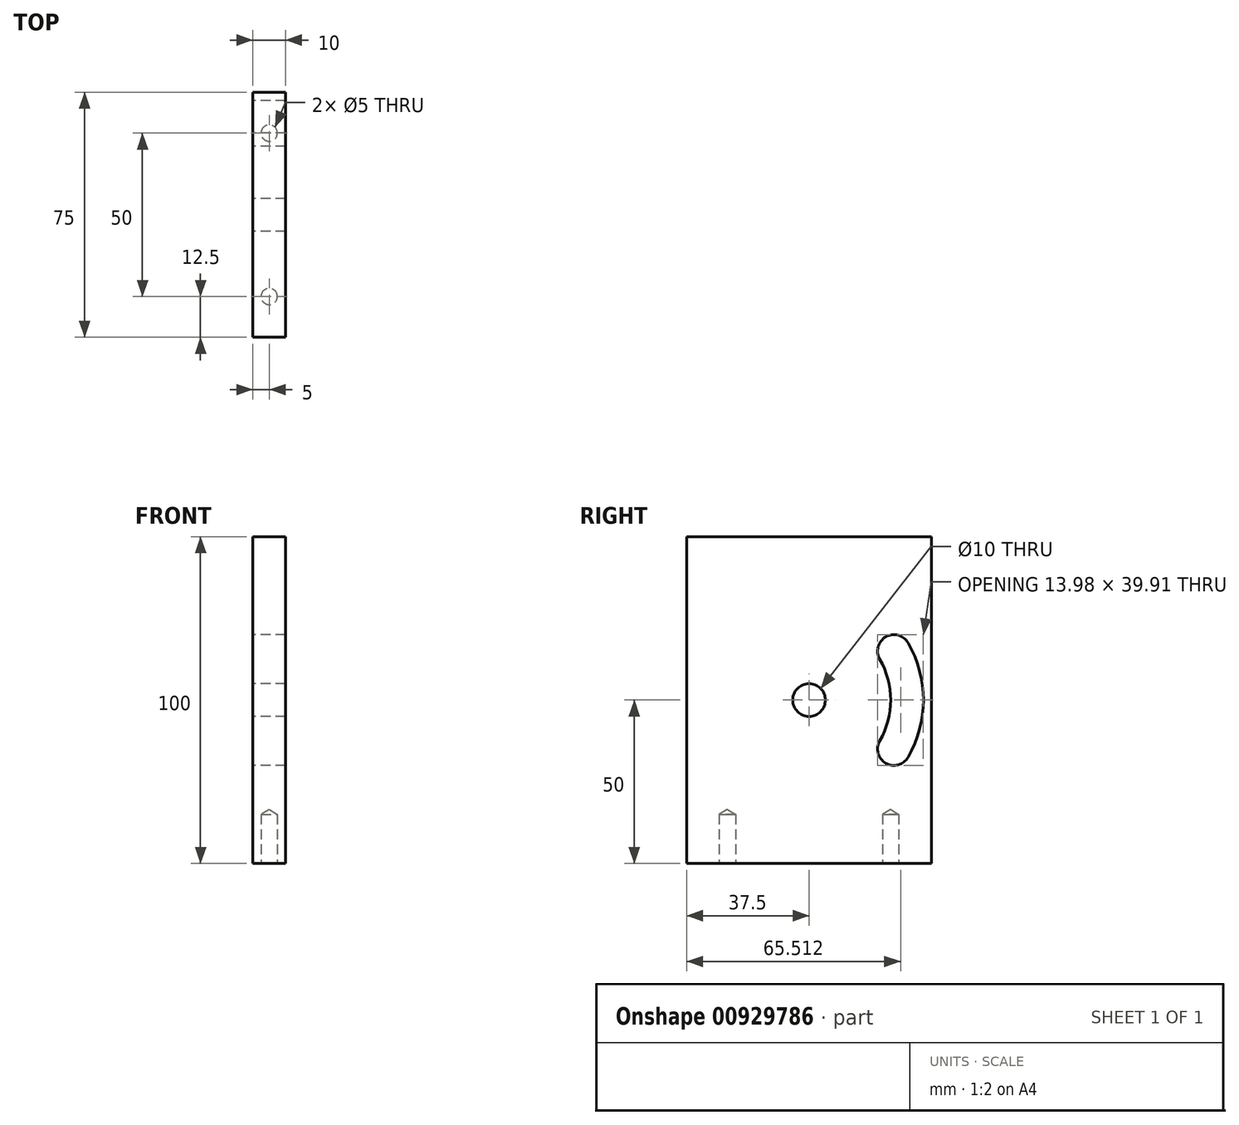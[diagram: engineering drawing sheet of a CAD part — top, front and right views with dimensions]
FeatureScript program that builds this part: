
annotation { "Feature Type Name" : "Feature", "Feature Type Description" : "" }
export const myFeature = defineFeature(function(context is Context, id is Id, definition is map)
    precondition{}
    {
        {
            var Q0;
            Q0=qCreatedBy(makeId("Top.planeOp"),FACE);
            var sketch = newSketch(context, id + "F0", { "sketchPlane" : qUnion([Q0])});
            skLineSegment(sketch, "E0.bottom", {"start": v(5, 37.5) * mm, "end": v(-5, 37.5) * mm});
            skLineSegment(sketch, "E0.top", {"start": v(5, -37.5) * mm, "end": v(-5, -37.5) * mm});
            skLineSegment(sketch, "E0.left", {"start": v(5, 37.5) * mm, "end": v(5, -37.5) * mm});
            skLineSegment(sketch, "E0.right", {"start": v(-5, 37.5) * mm, "end": v(-5, -37.5) * mm});
            skPoint(sketch, "E0.middle", {"position": v(0, 0) * mm});
            skSolve(sketch);
        }
        {
            var Q0;
            Q0 = qSketchRegion(id + "F0", true);
            extrude(context, id + "F1", {"entities" : qUnion([Q0]), "depth" : 100 * mm, "offsetDistance" : 25 * mm});
        }
        {
            var Q0;
            Q0=makeQuery(id+"F1.opExtrude","CAP_FACE",FACE,{"disambiguationData":[OSD([sQuery(id+"F0.wireOp",EDGE,"E0.bottom"),sQuery(id+"F0.wireOp",EDGE,"E0.top"),sQuery(id+"F0.wireOp",EDGE,"E0.left"),sQuery(id+"F0.wireOp",EDGE,"E0.right")])],"isStart":true});
            var sketch = newSketch(context, id + "F2", { "sketchPlane" : qUnion([Q0])});
            skLineSegment(sketch, "E1", {"start": v(0, 37.5) * mm, "end": v(0, -37.5) * mm, "construction": true});
            skLineSegment(sketch, "E2", {"start": v(-5, 0) * mm, "end": v(5, 0) * mm, "construction": true});
            skLineSegment(sketch, "E3.0", {"start": v(-7.5, -25) * mm, "end": v(7.5, -25) * mm, "construction": true});
            skLineSegment(sketch, "E4.0", {"start": v(-7.5, 25) * mm, "end": v(7.5, 25) * mm, "construction": true});
            skCircle(sketch, "E5", {"center": v(0, 25) * mm, "radius": 2.5 * mm});
            skCircle(sketch, "E6", {"center": v(0, -25) * mm, "radius": 2.5 * mm});
            skSolve(sketch);
        }
        {
            var Q0;
            Q0=sQuery(id+"F2.wireOp",VERTEX,"E5.center");
            var Q1;
            Q1=sQuery(id+"F2.wireOp",VERTEX,"E6.center");
            var Q2;
            Q2=makeQuery(id+"F1.opExtrude","SWEPT_BODY",BODY,{"disambiguationData":[OSD([sQuery(id+"F0.wireOp",EDGE,"E0.bottom"),sQuery(id+"F0.wireOp",EDGE,"E0.top"),sQuery(id+"F0.wireOp",EDGE,"E0.left"),sQuery(id+"F0.wireOp",EDGE,"E0.right")])]});
            hole(context, id + "F3", {"style" : HoleStyle.SIMPLE, "endStyle" : HoleEndStyle.BLIND, "standardTappedOrClearance" : lookupTablePath({ "standard" : "ISO", "engagement" : "75%", "pitch" : "1 mm", "size" : "M6", "type" : "Tapped" }), "standardBlindInLast" : lookupTablePath({ "standard" : "ISO", "engagement" : "75%", "pitch" : "1 mm", "size" : "M6", "type" : "Tapped" }), "holeDiameter" : 5 * mm, "majorDiameter" : 6 * mm, "showTappedDepth" : true, "holeDepth" : 15 * mm, "isTappedThrough" : true, "tappedDepth" : 12 * mm, "tapClearance" : 3, "locations" : qUnion([Q0, Q1]), "scope" : qUnion([Q2])});
        }
        {
            var Q0;
            Q0=makeQuery(id+"F1.opExtrude","SWEPT_FACE",FACE,{"disambiguationData":[OSD([sQuery(id+"F0.wireOp",EDGE,"E0.right")])]});
            var sketch = newSketch(context, id + "F4", { "sketchPlane" : qUnion([Q0])});
            skLineSegment(sketch, "E7", {"start": v(-37.5, 50) * mm, "end": v(37.5, 50) * mm, "construction": true});
            skLineSegment(sketch, "E8", {"start": v(0, 100) * mm, "end": v(0, 0) * mm, "construction": true});
            skCircle(sketch, "E9", {"center": v(0, 50) * mm, "radius": 5 * mm});
            skSolve(sketch);
        }
        {
            var Q0;
            Q0 = qSketchRegion(id + "F4", true);
            extrude(context, id + "F5", {"entities" : qUnion([Q0]), "operationType" : NewBodyOperationType.REMOVE, "endBound" : BoundingType.UP_TO_NEXT, "oppositeDirection" : true, "depth" : 25 * mm, "offsetDistance" : 25 * mm});
        }
        {
            var Q0;
            Q0=makeQuery(id+"F1.opExtrude","SWEPT_FACE",FACE,{"disambiguationData":[OSD([sQuery(id+"F0.wireOp",EDGE,"E0.right")])]});
            var sketch = newSketch(context, id + "F6", { "sketchPlane" : qUnion([Q0])});
            skLineSegment(sketch, "E10", {"start": v(-37.5, 50) * mm, "end": v(37.5, 50) * mm, "construction": true});
            skLineSegment(sketch, "E11", {"start": v(0, 100) * mm, "end": v(0, 0) * mm, "construction": true});
            skArc(sketch, "E12", {"start": v(-21.65, 62.5) * mm, "mid": v(-25, 50) * mm, "end": v(-21.65, 37.5) * mm});
            skArc(sketch, "E13.0", {"start": v(-30.31, 67.5) * mm, "mid": v(-35, 50) * mm, "end": v(-30.31, 32.5) * mm});
            skLineSegment(sketch, "E14.0", {"start": v(-42.5, -5) * mm, "end": v(42.5, -5) * mm});
            skLineSegment(sketch, "E14.1", {"start": v(-42.5, 105) * mm, "end": v(-42.5, -5) * mm});
            skLineSegment(sketch, "E14.2", {"start": v(42.5, 105) * mm, "end": v(-42.5, 105) * mm});
            skLineSegment(sketch, "E14.3", {"start": v(42.5, -5) * mm, "end": v(42.5, 105) * mm});
            skLineSegment(sketch, "E15", {"start": v(-21.65, 62.5) * mm, "end": v(-30.31, 67.5) * mm, "construction": true});
            skLineSegment(sketch, "E16.MirrorCS", {"start": v(-21.65, 37.5) * mm, "end": v(-30.31, 32.5) * mm, "construction": true});
            skPoint(sketch, "E17.orphan", {"position": v(-32.43, 68.72) * mm});
            skPoint(sketch, "E18.orphan", {"position": v(-32.43, 31.28) * mm});
            skArc(sketch, "E19", {"start": v(-21.65, 62.5) * mm, "mid": v(-23.48, 69.33) * mm, "end": v(-30.31, 67.5) * mm});
            skArc(sketch, "E20", {"start": v(-30.31, 32.5) * mm, "mid": v(-23.48, 30.67) * mm, "end": v(-21.65, 37.5) * mm});
            skSolve(sketch);
        }
        {
            var Q0;
            Q0=makeQuery(id+"F6.imprint","IMPRINT",FACE,{"disambiguationData":[TD([[makeQuery(id+"F6.imprint","IMPRINT",EDGE,{"derivedFrom":sQuery(id+"F6.wireOp",EDGE,"E12")}),-1.0]])]});
            var Q1;
            Q1=sQuery(id+"F6.wireOp",EDGE,"E12");
            var Q2;
            Q2=sQuery(id+"F6.wireOp",EDGE,"E19");
            var Q3;
            Q3=sQuery(id+"F6.wireOp",EDGE,"E13.0");
            var Q4;
            Q4=sQuery(id+"F6.wireOp",EDGE,"E20");
            extrude(context, id + "F7", {"entities" : qUnion([Q0]), "operationType" : NewBodyOperationType.REMOVE, "surfaceEntities" : qUnion([Q1, Q2, Q3, Q4]), "endBound" : BoundingType.UP_TO_NEXT, "oppositeDirection" : true, "depth" : 25 * mm, "offsetDistance" : 25 * mm});
        }
    });
